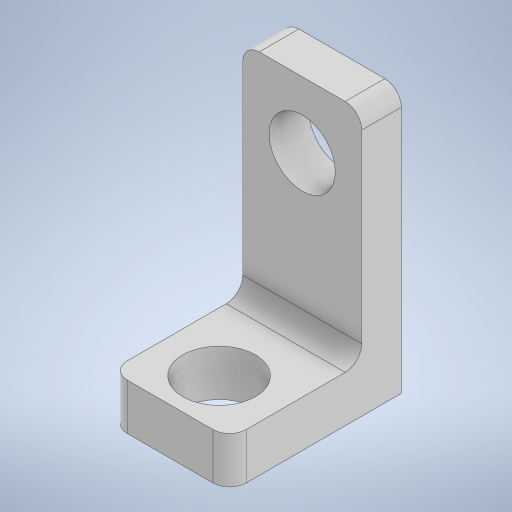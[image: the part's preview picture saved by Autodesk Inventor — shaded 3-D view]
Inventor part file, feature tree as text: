
AUTODESK INVENTOR PART (.ipt)
format: ipt  version: 2024 (Build 280153000, 153)  size: 619,008 bytes
history: native  units: mm
features: sketch x3, extrude x2, hole x1, fillet x1, projected_geometry x1
ambient origin geometry x8: Origin, YZ Plane, XZ Plane, XY Plane, X Axis, Y Axis, Z Axis, Center Point
bodies: Solid1 (feature_tree)
feature tree (8):
  extrude  "Extrusion1"  Depth=5.0mm
  extrude  "Extrusion2"  Depth=5.0mm
  hole  "Hole1"  [1 undecoded]
  fillet  "Fillet1"  Radius=3.0mm
  sketch  "Sketch1"  dims[d0=5.0mm d1=4.5mm]
  sketch  "Sketch2"  dims[d2=4.5mm d3=5.0mm]
  projected_geometry  "Projected Loop1"
  sketch  "Sketch3"  dims[d4=11.5mm d5=3.5mm d6=3.0mm d7=0.0mm d8=3.5mm d9=10.0mm d10=0.0mm d11=5.5mm d12=6.0mm d13=4.0mm d14=2.0mm d15=90.0deg d16=4.0mm d17=20.594885mm d18=1.25mm d19=0.5mm d20=0.872665mm d21=0.5mm d22=0.872665mm]
note: 1 required parameter value undecoded (feature->parameter linkage not recoverable at this tier; creation-order binding heuristic only, values carry confidence <= 0.55)
